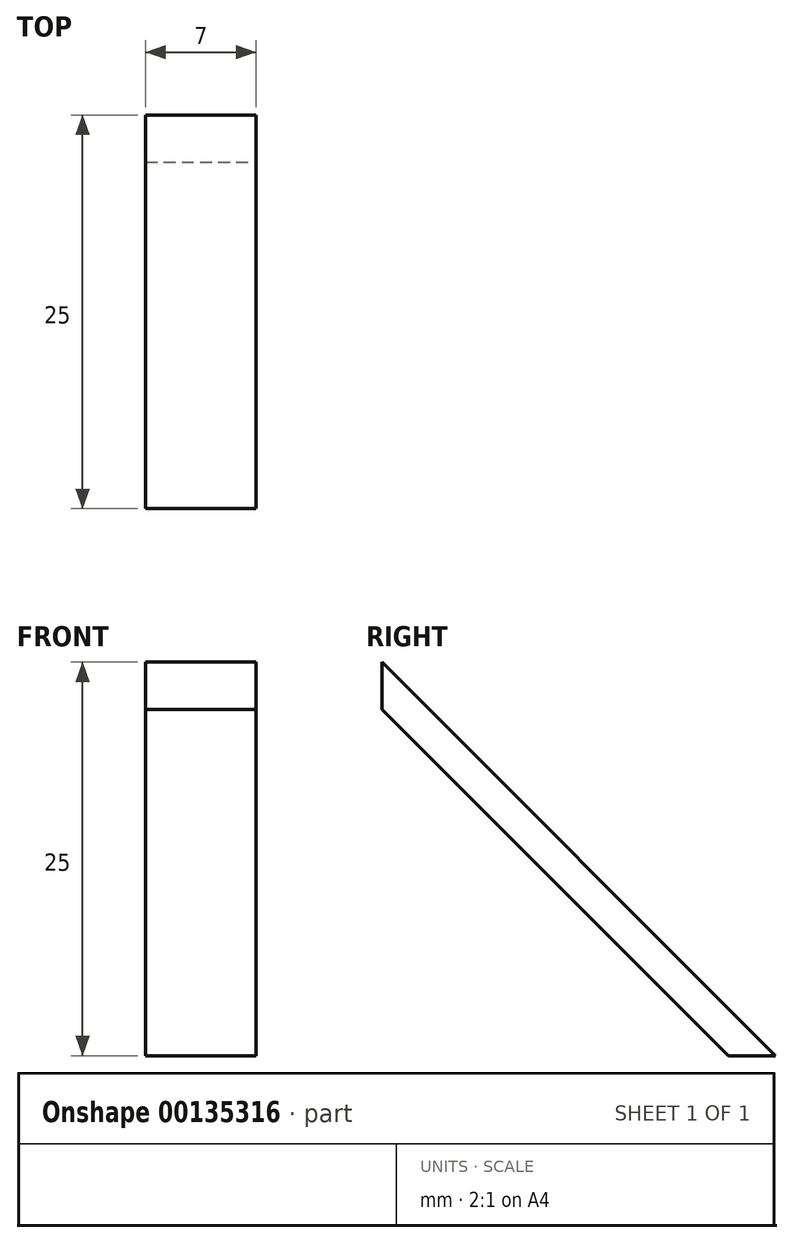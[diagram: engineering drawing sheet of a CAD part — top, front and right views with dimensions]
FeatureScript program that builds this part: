
annotation { "Feature Type Name" : "Feature", "Feature Type Description" : "" }
export const myFeature = defineFeature(function(context is Context, id is Id, definition is map)
    precondition{}
    {
        {
            var Q0;
            Q0=qCreatedBy(makeId("Right.planeOp"),FACE);
            var sketch = newSketch(context, id + "F0", { "sketchPlane" : qUnion([Q0])});
            skLineSegment(sketch, "E0", {"start": v(0, 0) * mm, "end": v(0, -3) * mm});
            skLineSegment(sketch, "E1", {"start": v(0, -3) * mm, "end": v(22, -25) * mm});
            skLineSegment(sketch, "E2", {"start": v(22, -25) * mm, "end": v(25, -25) * mm});
            skLineSegment(sketch, "E3", {"start": v(25, -25) * mm, "end": v(0, 0) * mm});
            skSolve(sketch);
        }
        {
            var Q0;
            Q0 = qSketchRegion(id + "F0", true);
            extrude(context, id + "F1", {"entities" : qUnion([Q0]), "oppositeDirection" : true, "depth" : 7 * mm});
        }
    });
